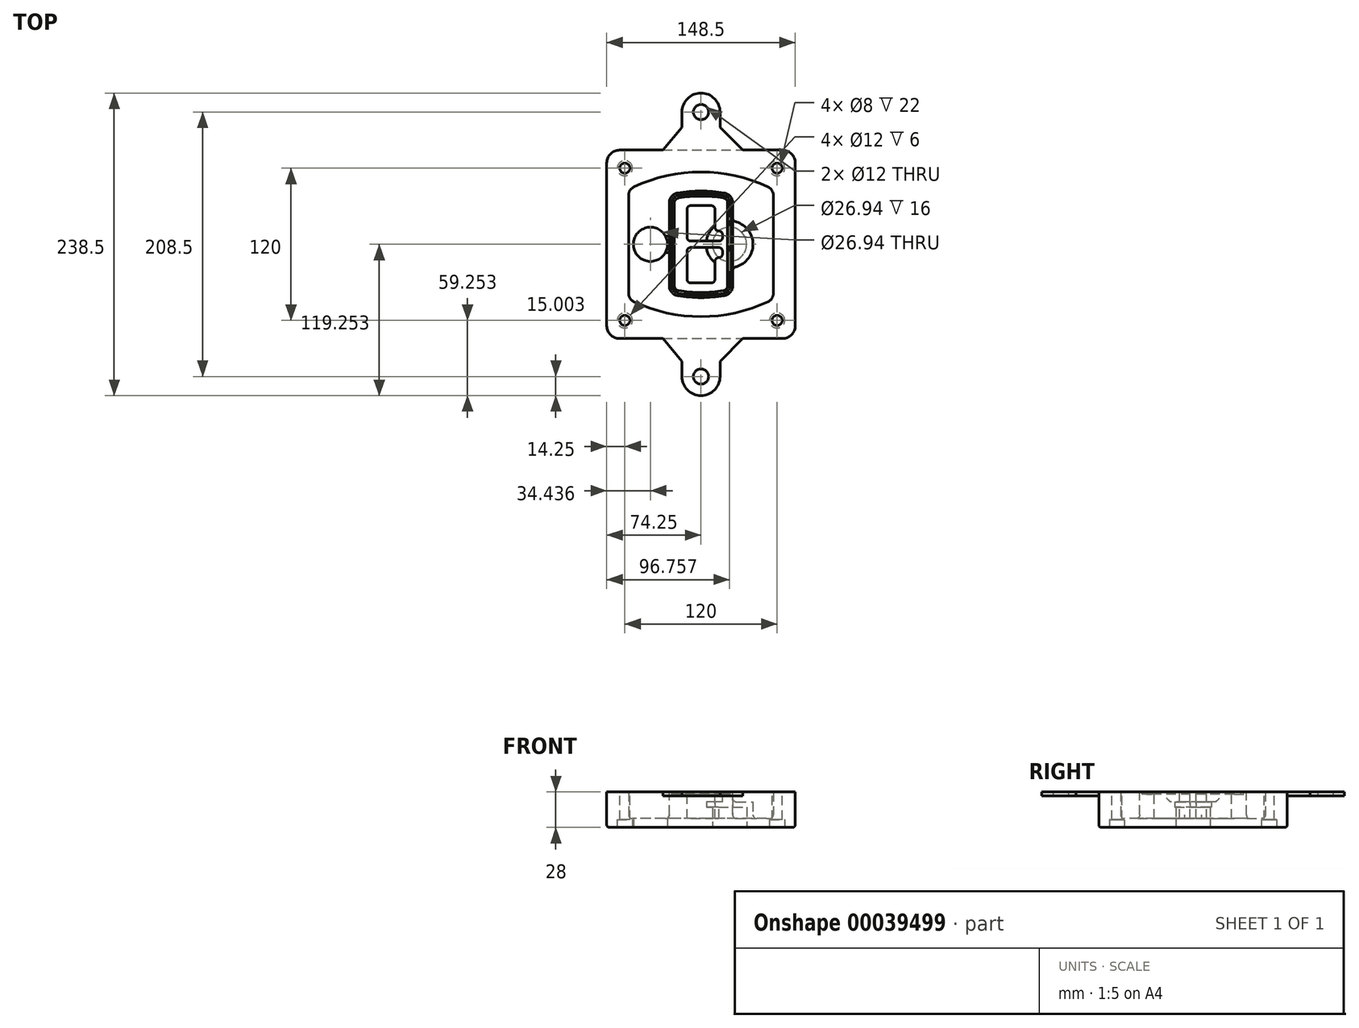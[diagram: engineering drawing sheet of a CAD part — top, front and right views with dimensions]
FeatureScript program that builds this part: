
annotation { "Feature Type Name" : "Feature", "Feature Type Description" : "" }
export const myFeature = defineFeature(function(context is Context, id is Id, definition is map)
    precondition{}
    {
        {
            var Q0;
            Q0=qCreatedBy(makeId("Top.planeOp"),FACE);
            var sketch = newSketch(context, id + "F0", { "sketchPlane" : qUnion([Q0])});
            skPoint(sketch, "E0.rect.middle", {"position": v(0, 0) * mm});
            skLineSegment(sketch, "E1.bottom", {"start": v(24.05, 28.38) * mm, "end": v(152.55, 28.38) * mm});
            skLineSegment(sketch, "E1.top", {"start": v(24.05, 176.88) * mm, "end": v(152.55, 176.88) * mm});
            skLineSegment(sketch, "E1.left", {"start": v(14.05, 38.38) * mm, "end": v(14.05, 166.88) * mm});
            skLineSegment(sketch, "E1.right", {"start": v(162.55, 38.38) * mm, "end": v(162.55, 166.88) * mm});
            skLineSegment(sketch, "E2", {"start": v(14.05, 176.88) * mm, "end": v(162.55, 28.38) * mm, "construction": true});
            skLineSegment(sketch, "E3", {"start": v(162.55, 176.88) * mm, "end": v(14.05, 28.38) * mm, "construction": true});
            skCircle(sketch, "E4", {"center": v(28.3, 162.63) * mm, "radius": 4 * mm});
            skCircle(sketch, "E5", {"center": v(148.3, 162.63) * mm, "radius": 4 * mm});
            skCircle(sketch, "E6", {"center": v(148.3, 42.63) * mm, "radius": 4 * mm});
            skCircle(sketch, "E7", {"center": v(28.3, 42.63) * mm, "radius": 4 * mm});
            skLineSegment(sketch, "E8", {"start": v(28.3, 162.63) * mm, "end": v(148.3, 162.63) * mm, "construction": true});
            skLineSegment(sketch, "E9", {"start": v(148.3, 162.63) * mm, "end": v(148.3, 42.63) * mm, "construction": true});
            skLineSegment(sketch, "E10", {"start": v(148.3, 42.63) * mm, "end": v(28.3, 42.63) * mm, "construction": true});
            skLineSegment(sketch, "E11", {"start": v(28.3, 42.63) * mm, "end": v(28.3, 162.63) * mm, "construction": true});
            skLineSegment(sketch, "E12", {"start": v(28.3, 141.46) * mm, "end": v(28.3, 63.8) * mm});
            skLineSegment(sketch, "E13", {"start": v(148.3, 141.46) * mm, "end": v(148.3, 63.8) * mm});
            skArc(sketch, "E14", {"start": v(142.56, 150.51) * mm, "mid": v(88.3, 162.63) * mm, "end": v(34.04, 150.51) * mm});
            skArc(sketch, "E15", {"start": v(34.04, 54.75) * mm, "mid": v(88.3, 42.63) * mm, "end": v(142.56, 54.75) * mm});
            skLineSegment(sketch, "E16", {"start": v(28.3, 102.63) * mm, "end": v(148.3, 102.63) * mm, "construction": true});
            skPoint(sketch, "E17.visualSharp", {"position": v(28.3, 57.63) * mm});
            skArc(sketch, "E17.filletArc", {"start": v(28.3, 63.8) * mm, "mid": v(29.86, 58.44) * mm, "end": v(34.04, 54.75) * mm});
            skPoint(sketch, "E18.visualSharp", {"position": v(28.3, 147.63) * mm});
            skArc(sketch, "E18.filletArc", {"start": v(34.04, 150.51) * mm, "mid": v(29.86, 146.82) * mm, "end": v(28.3, 141.46) * mm});
            skPoint(sketch, "E19.visualSharp", {"position": v(148.3, 147.63) * mm});
            skArc(sketch, "E19.filletArc", {"start": v(148.3, 141.46) * mm, "mid": v(146.74, 146.82) * mm, "end": v(142.56, 150.51) * mm});
            skPoint(sketch, "E20.visualSharp", {"position": v(148.3, 57.63) * mm});
            skArc(sketch, "E20.filletArc", {"start": v(142.56, 54.75) * mm, "mid": v(146.74, 58.44) * mm, "end": v(148.3, 63.8) * mm});
            skPoint(sketch, "E21.visualSharp", {"position": v(14.05, 176.88) * mm});
            skArc(sketch, "E21.filletArc", {"start": v(24.05, 176.88) * mm, "mid": v(16.98, 173.95) * mm, "end": v(14.05, 166.88) * mm});
            skPoint(sketch, "E22.visualSharp", {"position": v(162.55, 176.88) * mm});
            skArc(sketch, "E22.filletArc", {"start": v(162.55, 166.88) * mm, "mid": v(159.62, 173.95) * mm, "end": v(152.55, 176.88) * mm});
            skPoint(sketch, "E23.visualSharp", {"position": v(162.55, 28.38) * mm});
            skArc(sketch, "E23.filletArc", {"start": v(152.55, 28.38) * mm, "mid": v(159.62, 31.31) * mm, "end": v(162.55, 38.38) * mm});
            skPoint(sketch, "E24.visualSharp", {"position": v(14.05, 28.38) * mm});
            skArc(sketch, "E24.filletArc", {"start": v(14.05, 38.38) * mm, "mid": v(16.98, 31.31) * mm, "end": v(24.05, 28.38) * mm});
            skArc(sketch, "E25.0", {"start": v(145.3, 141.46) * mm, "mid": v(144.2, 145.22) * mm, "end": v(141.28, 147.8) * mm});
            skLineSegment(sketch, "E25.1", {"start": v(145.3, 141.46) * mm, "end": v(145.3, 63.8) * mm});
            skArc(sketch, "E25.2", {"start": v(141.28, 57.47) * mm, "mid": v(144.2, 60.05) * mm, "end": v(145.3, 63.8) * mm});
            skArc(sketch, "E25.3", {"start": v(35.32, 57.47) * mm, "mid": v(88.3, 45.63) * mm, "end": v(141.28, 57.47) * mm});
            skArc(sketch, "E25.4", {"start": v(31.3, 63.8) * mm, "mid": v(32.4, 60.05) * mm, "end": v(35.32, 57.47) * mm});
            skArc(sketch, "E25.5", {"start": v(141.28, 147.8) * mm, "mid": v(88.3, 159.63) * mm, "end": v(35.32, 147.8) * mm});
            skLineSegment(sketch, "E25.6", {"start": v(31.3, 141.46) * mm, "end": v(31.3, 63.8) * mm});
            skArc(sketch, "E25.7", {"start": v(35.32, 147.8) * mm, "mid": v(32.4, 145.22) * mm, "end": v(31.3, 141.46) * mm});
            skArc(sketch, "E26.0", {"start": v(32.34, 154.13) * mm, "mid": v(26.48, 148.97) * mm, "end": v(24.3, 141.46) * mm});
            skArc(sketch, "E26.1", {"start": v(144.26, 154.13) * mm, "mid": v(88.3, 166.63) * mm, "end": v(32.34, 154.13) * mm});
            skArc(sketch, "E26.2", {"start": v(152.3, 141.46) * mm, "mid": v(150.12, 148.97) * mm, "end": v(144.26, 154.13) * mm});
            skLineSegment(sketch, "E26.3", {"start": v(152.3, 141.46) * mm, "end": v(152.3, 63.8) * mm});
            skArc(sketch, "E26.4", {"start": v(144.26, 51.13) * mm, "mid": v(150.12, 56.3) * mm, "end": v(152.3, 63.8) * mm});
            skLineSegment(sketch, "E26.5", {"start": v(24.3, 141.46) * mm, "end": v(24.3, 63.8) * mm});
            skArc(sketch, "E26.6", {"start": v(32.34, 51.13) * mm, "mid": v(88.3, 38.63) * mm, "end": v(144.26, 51.13) * mm});
            skArc(sketch, "E26.7", {"start": v(24.3, 63.8) * mm, "mid": v(26.48, 56.3) * mm, "end": v(32.34, 51.13) * mm});
            skSolve(sketch);
        }
        {
            var Q0;
            Q0=makeQuery(id+"F0.imprint","IMPRINT",FACE,{"disambiguationData":[TD([[makeQuery(id+"F0.imprint","IMPRINT",EDGE,{"derivedFrom":sQuery(id+"F0.wireOp",EDGE,"E1.bottom")}),1.0]])]});
            var Q1;
            Q1=makeQuery(id+"F0.imprint","IMPRINT",FACE,{"disambiguationData":[TD([[makeQuery(id+"F0.imprint","IMPRINT",EDGE,{"derivedFrom":sQuery(id+"F0.wireOp",EDGE,"E12")}),1.0]])]});
            var Q2;
            Q2=makeQuery(id+"F0.imprint","IMPRINT",FACE,{"disambiguationData":[TD([[makeQuery(id+"F0.imprint","IMPRINT",EDGE,{"derivedFrom":sQuery(id+"F0.wireOp",EDGE,"E25.0")}),1.0]])]});
            var Q3;
            Q3=makeQuery(id+"F0.imprint","IMPRINT",FACE,{"disambiguationData":[TD([[makeQuery(id+"F0.imprint","IMPRINT",EDGE,{"derivedFrom":sQuery(id+"F0.wireOp",EDGE,"E12")}),-1.0]])]});
            extrude(context, id + "F1", {"entities" : qUnion([Q0, Q1, Q2, Q3]), "oppositeDirection" : true, "depth" : 25 * mm});
        }
        {
            var Q0;
            Q0=makeQuery(id+"F0.imprint","IMPRINT",FACE,{"disambiguationData":[TD([[makeQuery(id+"F0.imprint","IMPRINT",EDGE,{"derivedFrom":sQuery(id+"F0.wireOp",EDGE,"E12")}),1.0]])]});
            extrude(context, id + "F2", {"entities" : qUnion([Q0]), "operationType" : NewBodyOperationType.ADD, "depth" : 3 * mm});
        }
        {
            var Q0;
            Q0=makeQuery(id+"F0.imprint","IMPRINT",FACE,{"disambiguationData":[TD([[makeQuery(id+"F0.imprint","IMPRINT",EDGE,{"derivedFrom":sQuery(id+"F0.wireOp",EDGE,"E25.0")}),1.0]])]});
            extrude(context, id + "F3", {"entities" : qUnion([Q0]), "operationType" : NewBodyOperationType.REMOVE, "oppositeDirection" : true, "depth" : 18 * mm});
        }
        {
            var Q0;
            Q0=makeQuery(id+"F2.opExtrude","CAP_FACE",FACE,{"disambiguationData":[OSD([sQuery(id+"F0.wireOp",EDGE,"E12"),sQuery(id+"F0.wireOp",EDGE,"E13"),sQuery(id+"F0.wireOp",EDGE,"E14"),sQuery(id+"F0.wireOp",EDGE,"E15"),sQuery(id+"F0.wireOp",EDGE,"E17.filletArc"),sQuery(id+"F0.wireOp",EDGE,"E18.filletArc"),sQuery(id+"F0.wireOp",EDGE,"E19.filletArc"),sQuery(id+"F0.wireOp",EDGE,"E20.filletArc"),sQuery(id+"F0.wireOp",EDGE,"E25.0"),sQuery(id+"F0.wireOp",EDGE,"E25.1"),sQuery(id+"F0.wireOp",EDGE,"E25.2"),sQuery(id+"F0.wireOp",EDGE,"E25.3"),sQuery(id+"F0.wireOp",EDGE,"E25.4"),sQuery(id+"F0.wireOp",EDGE,"E25.5"),sQuery(id+"F0.wireOp",EDGE,"E25.6"),sQuery(id+"F0.wireOp",EDGE,"E25.7")])],"isStart":false});
            var sketch = newSketch(context, id + "F4", { "sketchPlane" : qUnion([Q0])});
            skArc(sketch, "E27.0", {"start": v(69.96, 62.18) * mm, "mid": v(88.3, 60.63) * mm, "end": v(106.64, 62.18) * mm});
            skArc(sketch, "E28.0", {"start": v(106.64, 143.09) * mm, "mid": v(88.3, 144.63) * mm, "end": v(69.96, 143.09) * mm});
            skLineSegment(sketch, "E29", {"start": v(63.3, 135.2) * mm, "end": v(63.3, 70.07) * mm});
            skLineSegment(sketch, "E30", {"start": v(113.3, 135.2) * mm, "end": v(113.3, 70.07) * mm});
            skLineSegment(sketch, "E31", {"start": v(63.3, 141.74) * mm, "end": v(113.3, 141.74) * mm, "construction": true});
            skLineSegment(sketch, "E32", {"start": v(63.3, 63.52) * mm, "end": v(113.3, 63.52) * mm, "construction": true});
            skPoint(sketch, "E33.visualSharp", {"position": v(63.3, 141.74) * mm});
            skArc(sketch, "E33.filletArc", {"start": v(69.96, 143.09) * mm, "mid": v(65.19, 140.36) * mm, "end": v(63.3, 135.2) * mm});
            skPoint(sketch, "E34.visualSharp", {"position": v(113.3, 141.74) * mm});
            skArc(sketch, "E34.filletArc", {"start": v(113.3, 135.2) * mm, "mid": v(111.41, 140.36) * mm, "end": v(106.64, 143.09) * mm});
            skPoint(sketch, "E35.visualSharp", {"position": v(113.3, 63.52) * mm});
            skArc(sketch, "E35.filletArc", {"start": v(106.64, 62.18) * mm, "mid": v(111.41, 64.9) * mm, "end": v(113.3, 70.07) * mm});
            skPoint(sketch, "E36.visualSharp", {"position": v(63.3, 63.52) * mm});
            skArc(sketch, "E36.filletArc", {"start": v(63.3, 70.07) * mm, "mid": v(65.19, 64.9) * mm, "end": v(69.96, 62.18) * mm});
            skArc(sketch, "E37.0", {"start": v(141.28, 147.8) * mm, "mid": v(88.3, 159.63) * mm, "end": v(35.32, 147.8) * mm});
            skArc(sketch, "E37.1", {"start": v(35.32, 147.8) * mm, "mid": v(32.4, 145.22) * mm, "end": v(31.3, 141.46) * mm});
            skLineSegment(sketch, "E37.2", {"start": v(31.3, 141.46) * mm, "end": v(31.3, 63.8) * mm});
            skArc(sketch, "E37.3", {"start": v(31.3, 63.8) * mm, "mid": v(32.4, 60.05) * mm, "end": v(35.32, 57.47) * mm});
            skArc(sketch, "E37.4", {"start": v(35.32, 57.47) * mm, "mid": v(88.3, 45.63) * mm, "end": v(141.28, 57.47) * mm});
            skArc(sketch, "E37.5", {"start": v(141.28, 57.47) * mm, "mid": v(144.2, 60.05) * mm, "end": v(145.3, 63.8) * mm});
            skLineSegment(sketch, "E37.6", {"start": v(145.3, 141.46) * mm, "end": v(145.3, 63.8) * mm});
            skArc(sketch, "E37.7", {"start": v(145.3, 141.46) * mm, "mid": v(144.2, 145.22) * mm, "end": v(141.28, 147.8) * mm});
            skLineSegment(sketch, "E38.0", {"start": v(111.3, 135.2) * mm, "end": v(111.3, 70.07) * mm});
            skArc(sketch, "E38.1", {"start": v(106.3, 64.15) * mm, "mid": v(109.88, 66.2) * mm, "end": v(111.3, 70.07) * mm});
            skArc(sketch, "E38.2", {"start": v(70.3, 64.15) * mm, "mid": v(88.3, 62.63) * mm, "end": v(106.3, 64.15) * mm});
            skArc(sketch, "E38.3", {"start": v(65.3, 70.07) * mm, "mid": v(66.72, 66.2) * mm, "end": v(70.3, 64.15) * mm});
            skLineSegment(sketch, "E38.4", {"start": v(65.3, 135.2) * mm, "end": v(65.3, 70.07) * mm});
            skArc(sketch, "E38.5", {"start": v(111.3, 135.2) * mm, "mid": v(109.88, 139.07) * mm, "end": v(106.3, 141.11) * mm});
            skArc(sketch, "E38.6", {"start": v(70.3, 141.11) * mm, "mid": v(66.72, 139.07) * mm, "end": v(65.3, 135.2) * mm});
            skArc(sketch, "E38.7", {"start": v(106.3, 141.11) * mm, "mid": v(88.3, 142.63) * mm, "end": v(70.3, 141.11) * mm});
            skArc(sketch, "E39.0", {"start": v(109.3, 135.2) * mm, "mid": v(108.36, 137.78) * mm, "end": v(105.97, 139.14) * mm});
            skLineSegment(sketch, "E39.1", {"start": v(109.3, 135.2) * mm, "end": v(109.3, 70.07) * mm});
            skArc(sketch, "E39.2", {"start": v(105.97, 66.12) * mm, "mid": v(108.36, 67.49) * mm, "end": v(109.3, 70.07) * mm});
            skArc(sketch, "E39.3", {"start": v(70.63, 66.12) * mm, "mid": v(88.3, 64.63) * mm, "end": v(105.97, 66.12) * mm});
            skArc(sketch, "E39.4", {"start": v(67.3, 70.07) * mm, "mid": v(68.24, 67.49) * mm, "end": v(70.63, 66.12) * mm});
            skArc(sketch, "E39.5", {"start": v(105.97, 139.14) * mm, "mid": v(88.3, 140.63) * mm, "end": v(70.63, 139.14) * mm});
            skLineSegment(sketch, "E39.6", {"start": v(67.3, 135.2) * mm, "end": v(67.3, 70.07) * mm});
            skArc(sketch, "E39.7", {"start": v(70.63, 139.14) * mm, "mid": v(68.24, 137.78) * mm, "end": v(67.3, 135.2) * mm});
            skLineSegment(sketch, "E40", {"start": v(63.3, 102.63) * mm, "end": v(113.3, 102.63) * mm, "construction": true});
            skLineSegment(sketch, "E41", {"start": v(77.3, 108.13) * mm, "end": v(77.3, 130.13) * mm});
            skLineSegment(sketch, "E42", {"start": v(80.3, 133.13) * mm, "end": v(96.3, 133.13) * mm});
            skLineSegment(sketch, "E43", {"start": v(99.3, 130.13) * mm, "end": v(99.3, 116.13) * mm});
            skLineSegment(sketch, "E44", {"start": v(102.3, 113.13) * mm, "end": v(102.3, 113.13) * mm});
            skLineSegment(sketch, "E45", {"start": v(105.3, 110.13) * mm, "end": v(105.3, 108.13) * mm});
            skLineSegment(sketch, "E46", {"start": v(102.3, 105.13) * mm, "end": v(80.3, 105.13) * mm});
            skPoint(sketch, "E47.visualSharp", {"position": v(77.3, 133.13) * mm});
            skArc(sketch, "E47.filletArc", {"start": v(80.3, 133.13) * mm, "mid": v(78.18, 132.25) * mm, "end": v(77.3, 130.13) * mm});
            skPoint(sketch, "E48.visualSharp", {"position": v(99.3, 133.13) * mm});
            skArc(sketch, "E48.filletArc", {"start": v(99.3, 130.13) * mm, "mid": v(98.42, 132.25) * mm, "end": v(96.3, 133.13) * mm});
            skPoint(sketch, "E49.visualSharp", {"position": v(99.3, 113.13) * mm});
            skArc(sketch, "E49.filletArc", {"start": v(99.3, 116.13) * mm, "mid": v(100.18, 114.01) * mm, "end": v(102.3, 113.13) * mm});
            skPoint(sketch, "E50.visualSharp", {"position": v(105.3, 113.13) * mm});
            skArc(sketch, "E50.filletArc", {"start": v(105.3, 110.13) * mm, "mid": v(104.42, 112.25) * mm, "end": v(102.3, 113.13) * mm});
            skPoint(sketch, "E51.visualSharp", {"position": v(105.3, 105.13) * mm});
            skArc(sketch, "E51.filletArc", {"start": v(102.3, 105.13) * mm, "mid": v(104.42, 106.01) * mm, "end": v(105.3, 108.13) * mm});
            skPoint(sketch, "E52.visualSharp", {"position": v(77.3, 105.13) * mm});
            skArc(sketch, "E52.filletArc", {"start": v(77.3, 108.13) * mm, "mid": v(78.18, 106.01) * mm, "end": v(80.3, 105.13) * mm});
            skLineSegment(sketch, "E53.0.MirrorCS", {"start": v(102.3, 100.13) * mm, "end": v(80.3, 100.13) * mm});
            skArc(sketch, "E54.0.MirrorCS", {"start": v(77.3, 97.13) * mm, "mid": v(78.18, 99.25) * mm, "end": v(80.3, 100.13) * mm});
            skLineSegment(sketch, "E55.0.MirrorCS", {"start": v(77.3, 97.13) * mm, "end": v(77.3, 75.13) * mm});
            skArc(sketch, "E56.0.MirrorCS", {"start": v(80.3, 72.13) * mm, "mid": v(78.18, 73.01) * mm, "end": v(77.3, 75.13) * mm});
            skLineSegment(sketch, "E57.0.MirrorCS", {"start": v(80.3, 72.13) * mm, "end": v(96.3, 72.13) * mm});
            skArc(sketch, "E58.0.MirrorCS", {"start": v(99.3, 75.13) * mm, "mid": v(98.42, 73.01) * mm, "end": v(96.3, 72.13) * mm});
            skLineSegment(sketch, "E59.0.MirrorCS", {"start": v(99.3, 75.13) * mm, "end": v(99.3, 89.13) * mm});
            skArc(sketch, "E60.0.MirrorCS", {"start": v(99.3, 89.13) * mm, "mid": v(100.18, 91.25) * mm, "end": v(102.3, 92.13) * mm});
            skArc(sketch, "E61.0.MirrorCS", {"start": v(105.3, 95.13) * mm, "mid": v(104.42, 93.01) * mm, "end": v(102.3, 92.13) * mm});
            skLineSegment(sketch, "E62.0.MirrorCS", {"start": v(105.3, 95.13) * mm, "end": v(105.3, 97.13) * mm});
            skArc(sketch, "E63.0.MirrorCS", {"start": v(102.3, 100.13) * mm, "mid": v(104.42, 99.25) * mm, "end": v(105.3, 97.13) * mm});
            skSolve(sketch);
        }
        {
            var Q0;
            Q0=makeQuery(id+"F4.imprint","IMPRINT",FACE,{"disambiguationData":[TD([[makeQuery(id+"F4.imprint","IMPRINT",EDGE,{"derivedFrom":sQuery(id+"F4.wireOp",EDGE,"E27.0")}),1.0]])]});
            var Q1;
            Q1=makeQuery(id+"F4.imprint","IMPRINT",FACE,{"disambiguationData":[TD([[makeQuery(id+"F4.imprint","IMPRINT",EDGE,{"derivedFrom":sQuery(id+"F4.wireOp",EDGE,"E38.0")}),-1.0]])]});
            var Q2;
            Q2=makeQuery(id+"F4.imprint","IMPRINT",FACE,{"disambiguationData":[TD([[makeQuery(id+"F4.imprint","IMPRINT",EDGE,{"derivedFrom":sQuery(id+"F4.wireOp",EDGE,"E39.0")}),1.0]])]});
            extrude(context, id + "F5", {"entities" : qUnion([Q0, Q1, Q2]), "operationType" : NewBodyOperationType.ADD, "endBound" : BoundingType.UP_TO_NEXT, "oppositeDirection" : true, "depth" : 25 * mm});
        }
        {
            var Q0;
            Q0=makeQuery(id+"F4.imprint","IMPRINT",FACE,{"disambiguationData":[TD([[makeQuery(id+"F4.imprint","IMPRINT",EDGE,{"derivedFrom":sQuery(id+"F4.wireOp",EDGE,"E38.0")}),-1.0]])]});
            extrude(context, id + "F6", {"entities" : qUnion([Q0]), "operationType" : NewBodyOperationType.REMOVE, "oppositeDirection" : true, "depth" : 2 * mm});
        }
        {
            var Q0;
            Q0=makeQuery(id+"F1.opExtrude","CAP_FACE",FACE,{"disambiguationData":[OSD([sQuery(id+"F0.wireOp",EDGE,"E1.bottom"),sQuery(id+"F0.wireOp",EDGE,"E1.top"),sQuery(id+"F0.wireOp",EDGE,"E1.left"),sQuery(id+"F0.wireOp",EDGE,"E1.right"),sQuery(id+"F0.wireOp",EDGE,"E4"),sQuery(id+"F0.wireOp",EDGE,"E5"),sQuery(id+"F0.wireOp",EDGE,"E6"),sQuery(id+"F0.wireOp",EDGE,"E7"),sQuery(id+"F0.wireOp",EDGE,"E21.filletArc"),sQuery(id+"F0.wireOp",EDGE,"E22.filletArc"),sQuery(id+"F0.wireOp",EDGE,"E23.filletArc"),sQuery(id+"F0.wireOp",EDGE,"E24.filletArc")])],"isStart":false});
            var sketch = newSketch(context, id + "F7", { "sketchPlane" : qUnion([Q0])});
            skCircle(sketch, "E64", {"center": v(110.8, -102.63) * mm, "radius": 13.47 * mm});
            skCircle(sketch, "E65", {"center": v(48.49, -102.63) * mm, "radius": 13.47 * mm});
            skLineSegment(sketch, "E66", {"start": v(162.55, -102.63) * mm, "end": v(14.05, -102.63) * mm});
            skCircle(sketch, "E67", {"center": v(110.8, -102.63) * mm, "radius": 18.47 * mm});
            skCircle(sketch, "E68", {"center": v(148.3, -162.63) * mm, "radius": 6 * mm});
            skCircle(sketch, "E69", {"center": v(28.3, -162.63) * mm, "radius": 6 * mm});
            skCircle(sketch, "E70", {"center": v(28.3, -42.63) * mm, "radius": 6 * mm});
            skCircle(sketch, "E71", {"center": v(148.3, -42.63) * mm, "radius": 6 * mm});
            skSolve(sketch);
        }
        {
            var Q0;
            {var subQ1=sQuery(id+"F7.wireOp",EDGE,"E66");var subQ4=sQuery(id+"F7.wireOp",EDGE,"E64");var subQ6=makeQuery(id+"F7.imprint","INTERSECT",VERTEX,{"disambiguationData":[OD(0.0)],"derivedFrom":[subQ4,subQ1]});Q0=makeQuery(id+"F7.imprint","IMPRINT",FACE,{"disambiguationData":[TD([[makeQuery(id+"F7.imprint","IMPRINT",EDGE,{"disambiguationData":[TD([[subQ6,-1.0]])],"derivedFrom":subQ4}),-1.0]])]});}
            var Q1;
            {var subQ0=sQuery(id+"F7.wireOp",EDGE,"E66");var subQ1=sQuery(id+"F7.wireOp",EDGE,"E64");var subQ3=makeQuery(id+"F7.imprint","INTERSECT",VERTEX,{"disambiguationData":[OD(0.0)],"derivedFrom":[subQ1,subQ0]});Q1=makeQuery(id+"F7.imprint","IMPRINT",FACE,{"disambiguationData":[TD([[makeQuery(id+"F7.imprint","IMPRINT",EDGE,{"disambiguationData":[TD([[subQ3,-1.0]])],"derivedFrom":subQ1}),1.0]])]});}
            var Q2;
            {var subQ0=sQuery(id+"F7.wireOp",EDGE,"E66");var subQ1=sQuery(id+"F7.wireOp",EDGE,"E64");var subQ3=makeQuery(id+"F7.imprint","INTERSECT",VERTEX,{"disambiguationData":[OD(0.0)],"derivedFrom":[subQ1,subQ0]});Q2=makeQuery(id+"F7.imprint","IMPRINT",FACE,{"disambiguationData":[TD([[makeQuery(id+"F7.imprint","IMPRINT",EDGE,{"disambiguationData":[TD([[subQ3,1.0]])],"derivedFrom":subQ1}),1.0]])]});}
            var Q3;
            {var subQ1=sQuery(id+"F7.wireOp",EDGE,"E66");var subQ4=sQuery(id+"F7.wireOp",EDGE,"E64");var subQ6=makeQuery(id+"F7.imprint","INTERSECT",VERTEX,{"disambiguationData":[OD(0.0)],"derivedFrom":[subQ4,subQ1]});Q3=makeQuery(id+"F7.imprint","IMPRINT",FACE,{"disambiguationData":[TD([[makeQuery(id+"F7.imprint","IMPRINT",EDGE,{"disambiguationData":[TD([[subQ6,1.0]])],"derivedFrom":subQ4}),-1.0]])]});}
            extrude(context, id + "F8", {"entities" : qUnion([Q0, Q1, Q2, Q3]), "operationType" : NewBodyOperationType.ADD, "oppositeDirection" : true, "depth" : 20 * mm});
        }
        {
            var Q0;
            {var subQ0=sQuery(id+"F7.wireOp",EDGE,"E66");var subQ1=sQuery(id+"F7.wireOp",EDGE,"E64");var subQ3=makeQuery(id+"F7.imprint","INTERSECT",VERTEX,{"disambiguationData":[OD(0.0)],"derivedFrom":[subQ1,subQ0]});Q0=makeQuery(id+"F7.imprint","IMPRINT",FACE,{"disambiguationData":[TD([[makeQuery(id+"F7.imprint","IMPRINT",EDGE,{"disambiguationData":[TD([[subQ3,-1.0]])],"derivedFrom":subQ1}),1.0]])]});}
            var Q1;
            {var subQ0=sQuery(id+"F7.wireOp",EDGE,"E66");var subQ1=sQuery(id+"F7.wireOp",EDGE,"E64");var subQ3=makeQuery(id+"F7.imprint","INTERSECT",VERTEX,{"disambiguationData":[OD(0.0)],"derivedFrom":[subQ1,subQ0]});Q1=makeQuery(id+"F7.imprint","IMPRINT",FACE,{"disambiguationData":[TD([[makeQuery(id+"F7.imprint","IMPRINT",EDGE,{"disambiguationData":[TD([[subQ3,1.0]])],"derivedFrom":subQ1}),1.0]])]});}
            extrude(context, id + "F9", {"entities" : qUnion([Q0, Q1]), "operationType" : NewBodyOperationType.REMOVE, "oppositeDirection" : true, "depth" : 16 * mm});
        }
        {
            var Q0;
            {var subQ0=sQuery(id+"F7.wireOp",EDGE,"E66");var subQ1=sQuery(id+"F7.wireOp",EDGE,"E65");var subQ3=makeQuery(id+"F7.imprint","INTERSECT",VERTEX,{"disambiguationData":[OD(0.0)],"derivedFrom":[subQ1,subQ0]});Q0=makeQuery(id+"F7.imprint","IMPRINT",FACE,{"disambiguationData":[TD([[makeQuery(id+"F7.imprint","IMPRINT",EDGE,{"disambiguationData":[TD([[subQ3,-1.0]])],"derivedFrom":subQ1}),1.0]])]});}
            var Q1;
            {var subQ0=sQuery(id+"F7.wireOp",EDGE,"E66");var subQ1=sQuery(id+"F7.wireOp",EDGE,"E65");var subQ3=makeQuery(id+"F7.imprint","INTERSECT",VERTEX,{"disambiguationData":[OD(0.0)],"derivedFrom":[subQ1,subQ0]});Q1=makeQuery(id+"F7.imprint","IMPRINT",FACE,{"disambiguationData":[TD([[makeQuery(id+"F7.imprint","IMPRINT",EDGE,{"disambiguationData":[TD([[subQ3,1.0]])],"derivedFrom":subQ1}),1.0]])]});}
            extrude(context, id + "F10", {"entities" : qUnion([Q0, Q1]), "operationType" : NewBodyOperationType.REMOVE, "oppositeDirection" : true, "depth" : 25 * mm});
        }
        {
            var Q0;
            Q0=makeQuery(id+"F7.imprint","IMPRINT",FACE,{"disambiguationData":[TD([[makeQuery(id+"F7.imprint","IMPRINT",EDGE,{"derivedFrom":sQuery(id+"F7.wireOp",EDGE,"E68")}),1.0]])]});
            var Q1;
            Q1=makeQuery(id+"F7.imprint","IMPRINT",FACE,{"disambiguationData":[TD([[makeQuery(id+"F7.imprint","IMPRINT",EDGE,{"derivedFrom":makeQuery(id+"F1.opExtrude","CAP_EDGE",EDGE,{"disambiguationData":[OSD([sQuery(id+"F0.wireOp",EDGE,"E5")])],"isStart":false})}),-1.0]])]});
            var Q2;
            Q2=makeQuery(id+"F7.imprint","IMPRINT",FACE,{"disambiguationData":[TD([[makeQuery(id+"F7.imprint","IMPRINT",EDGE,{"derivedFrom":sQuery(id+"F7.wireOp",EDGE,"E69")}),1.0]])]});
            var Q3;
            Q3=makeQuery(id+"F7.imprint","IMPRINT",FACE,{"disambiguationData":[TD([[makeQuery(id+"F7.imprint","IMPRINT",EDGE,{"derivedFrom":makeQuery(id+"F1.opExtrude","CAP_EDGE",EDGE,{"disambiguationData":[OSD([sQuery(id+"F0.wireOp",EDGE,"E4")])],"isStart":false})}),-1.0]])]});
            var Q4;
            Q4=makeQuery(id+"F7.imprint","IMPRINT",FACE,{"disambiguationData":[TD([[makeQuery(id+"F7.imprint","IMPRINT",EDGE,{"derivedFrom":sQuery(id+"F7.wireOp",EDGE,"E70")}),1.0]])]});
            var Q5;
            Q5=makeQuery(id+"F7.imprint","IMPRINT",FACE,{"disambiguationData":[TD([[makeQuery(id+"F7.imprint","IMPRINT",EDGE,{"derivedFrom":makeQuery(id+"F1.opExtrude","CAP_EDGE",EDGE,{"disambiguationData":[OSD([sQuery(id+"F0.wireOp",EDGE,"E7")])],"isStart":false})}),-1.0]])]});
            var Q6;
            Q6=makeQuery(id+"F7.imprint","IMPRINT",FACE,{"disambiguationData":[TD([[makeQuery(id+"F7.imprint","IMPRINT",EDGE,{"derivedFrom":sQuery(id+"F7.wireOp",EDGE,"E71")}),1.0]])]});
            var Q7;
            Q7=makeQuery(id+"F7.imprint","IMPRINT",FACE,{"disambiguationData":[TD([[makeQuery(id+"F7.imprint","IMPRINT",EDGE,{"derivedFrom":makeQuery(id+"F1.opExtrude","CAP_EDGE",EDGE,{"disambiguationData":[OSD([sQuery(id+"F0.wireOp",EDGE,"E6")])],"isStart":false})}),-1.0]])]});
            extrude(context, id + "F11", {"entities" : qUnion([Q0, Q1, Q2, Q3, Q4, Q5, Q6, Q7]), "operationType" : NewBodyOperationType.REMOVE, "oppositeDirection" : true, "depth" : 6 * mm});
        }
        {
            var Q0;
            Q0=makeQuery(id+"F9.boolean.opBoolean","COPY",FACE,{"derivedFrom":makeQuery(id+"F9.opExtrude","CAP_FACE",FACE,{"disambiguationData":[OSD([sQuery(id+"F7.wireOp",EDGE,"E64")])],"isStart":false})});
            var sketch = newSketch(context, id + "F12", { "sketchPlane" : qUnion([Q0])});
            skArc(sketch, "E72.0", {"start": v(99.3, -88.19) * mm, "mid": v(94.75, -93.5) * mm, "end": v(92.5, -100.13) * mm});
            skArc(sketch, "E72.1", {"start": v(92.5, -105.13) * mm, "mid": v(94.75, -111.76) * mm, "end": v(99.3, -117.08) * mm});
            skLineSegment(sketch, "E73", {"start": v(92.5, -105.13) * mm, "end": v(102.3, -105.13) * mm});
            skLineSegment(sketch, "E74.0", {"start": v(102.3, -100.13) * mm, "end": v(92.5, -100.13) * mm});
            skArc(sketch, "E74.1", {"start": v(102.3, -100.13) * mm, "mid": v(104.42, -99.25) * mm, "end": v(105.3, -97.13) * mm});
            skLineSegment(sketch, "E74.2", {"start": v(105.3, -95.13) * mm, "end": v(105.3, -97.13) * mm});
            skArc(sketch, "E74.3", {"start": v(105.3, -95.13) * mm, "mid": v(104.42, -93.01) * mm, "end": v(102.3, -92.13) * mm});
            skArc(sketch, "E74.4", {"start": v(99.3, -89.13) * mm, "mid": v(100.18, -91.25) * mm, "end": v(102.3, -92.13) * mm});
            skLineSegment(sketch, "E74.5", {"start": v(99.3, -88.19) * mm, "end": v(99.3, -89.13) * mm});
            skLineSegment(sketch, "E74.7", {"start": v(102.3, -105.13) * mm, "end": v(92.5, -105.13) * mm});
            skArc(sketch, "E74.8", {"start": v(102.3, -105.13) * mm, "mid": v(104.42, -106.01) * mm, "end": v(105.3, -108.13) * mm});
            skLineSegment(sketch, "E74.9", {"start": v(105.3, -110.13) * mm, "end": v(105.3, -108.13) * mm});
            skArc(sketch, "E74.10", {"start": v(105.3, -110.13) * mm, "mid": v(104.42, -112.25) * mm, "end": v(102.3, -113.13) * mm});
            skArc(sketch, "E74.11", {"start": v(99.3, -116.13) * mm, "mid": v(100.18, -114.01) * mm, "end": v(102.3, -113.13) * mm});
            skLineSegment(sketch, "E74.12", {"start": v(99.3, -117.08) * mm, "end": v(99.3, -116.13) * mm});
            skPoint(sketch, "E75.orphan", {"position": v(99.3, -130.13) * mm});
            skPoint(sketch, "E76.orphan", {"position": v(80.3, -105.13) * mm});
            skPoint(sketch, "E77.orphan", {"position": v(80.3, -100.13) * mm});
            skPoint(sketch, "E78.orphan", {"position": v(99.3, -75.13) * mm});
            skSolve(sketch);
        }
        {
            var Q0;
            {var subQ7=sQuery(id+"F12.wireOp",EDGE,"E72.0");var subQ14=sQuery(id+"F12.wireOp",EDGE,"E72.1");var subQ16=sQuery(id+"F12.wireOp",EDGE,"E74.1");var subQ18=sQuery(id+"F12.wireOp",EDGE,"E74.8");Q0=qUnion([makeQuery(id+"F12.imprint","IMPRINT",FACE,{"disambiguationData":[TD([[makeQuery(id+"F12.imprint","IMPRINT",EDGE,{"derivedFrom":subQ7}),1.0]])]}),makeQuery(id+"F12.imprint","IMPRINT",FACE,{"disambiguationData":[TD([[makeQuery(id+"F12.imprint","IMPRINT",EDGE,{"derivedFrom":subQ14}),1.0]])]}),makeQuery(id+"F12.imprint","IMPRINT",FACE,{"disambiguationData":[TD([[makeQuery(id+"F12.imprint","IMPRINT",EDGE,{"derivedFrom":subQ16}),1.0]])]}),makeQuery(id+"F12.imprint","IMPRINT",FACE,{"disambiguationData":[TD([[makeQuery(id+"F12.imprint","IMPRINT",EDGE,{"derivedFrom":subQ18}),-1.0]])]})]);}
            var Q1;
            Q1=makeQuery(id+"F5.boolean.opBoolean","SPLIT",FACE,{"disambiguationData":[TD([makeQuery(id+"F5.opExtrude","SWEPT_FACE",FACE,{"disambiguationData":[OSD([sQuery(id+"F4.wireOp",EDGE,"E41")])]})])],"derivedFrom":makeQuery(id+"F3.boolean.opBoolean","COPY",FACE,{"derivedFrom":makeQuery(id+"F3.opExtrude","CAP_FACE",FACE,{"disambiguationData":[OSD([sQuery(id+"F0.wireOp",EDGE,"E25.0"),sQuery(id+"F0.wireOp",EDGE,"E25.1"),sQuery(id+"F0.wireOp",EDGE,"E25.2"),sQuery(id+"F0.wireOp",EDGE,"E25.3"),sQuery(id+"F0.wireOp",EDGE,"E25.4"),sQuery(id+"F0.wireOp",EDGE,"E25.5"),sQuery(id+"F0.wireOp",EDGE,"E25.6"),sQuery(id+"F0.wireOp",EDGE,"E25.7")])],"isStart":false})})});
            extrude(context, id + "F13", {"entities" : qUnion([Q0]), "operationType" : NewBodyOperationType.REMOVE, "endBound" : BoundingType.UP_TO_SURFACE, "endBoundEntityFace" : qUnion([Q1]), "depth" : 25 * mm});
        }
        {
            var Q0;
            Q0=makeQuery(id+"F3.boolean.opBoolean","COPY",EDGE,{"derivedFrom":makeQuery(id+"F3.opExtrude","CAP_EDGE",EDGE,{"disambiguationData":[OSD([sQuery(id+"F0.wireOp",EDGE,"E25.6")])],"isStart":false})});
            var Q1;
            Q1=makeQuery(id+"F8.boolean.opBoolean","INTERSECT",EDGE,{"derivedFrom":[makeQuery(id+"F5.opExtrude","SWEPT_FACE",FACE,{"disambiguationData":[OSD([sQuery(id+"F4.wireOp",EDGE,"E30")])]}),makeQuery(id+"F8.opExtrude","CAP_FACE",FACE,{"disambiguationData":[OSD([sQuery(id+"F7.wireOp",EDGE,"E67")])],"isStart":false})]});
            var Q2;
            Q2=makeQuery(id+"F8.boolean.opBoolean","INTERSECT",EDGE,{"disambiguationData":[OD(1.0)],"derivedFrom":[makeQuery(id+"F5.opExtrude","SWEPT_FACE",FACE,{"disambiguationData":[OSD([sQuery(id+"F4.wireOp",EDGE,"E30")])]}),makeQuery(id+"F8.opExtrude","SWEPT_FACE",FACE,{"disambiguationData":[OSD([sQuery(id+"F7.wireOp",EDGE,"E67")])]})]});
            var Q3;
            {var subQ0=sQuery(id+"F4.wireOp",EDGE,"E30");Q3=makeQuery(id+"F8.boolean.opBoolean","SPLIT",EDGE,{"disambiguationData":[TD([makeQuery(id+"F5.opExtrude","SWEPT_FACE",FACE,{"disambiguationData":[OSD([sQuery(id+"F4.wireOp",EDGE,"E35.filletArc")])]})])],"derivedFrom":makeQuery(id+"F5.opExtrude","CAP_EDGE",EDGE,{"disambiguationData":[OSD([subQ0])],"isStart":false})});}
            var Q4;
            {var subQ0=sQuery(id+"F0.wireOp",EDGE,"E25.7");var subQ1=sQuery(id+"F0.wireOp",EDGE,"E25.1");var subQ2=sQuery(id+"F0.wireOp",EDGE,"E25.6");var subQ3=sQuery(id+"F0.wireOp",EDGE,"E25.5");var subQ4=sQuery(id+"F0.wireOp",EDGE,"E25.4");var subQ5=sQuery(id+"F0.wireOp",EDGE,"E25.0");var subQ6=sQuery(id+"F0.wireOp",EDGE,"E25.2");var subQ7=sQuery(id+"F0.wireOp",EDGE,"E25.3");Q4=makeQuery(id+"F8.boolean.opBoolean","INTERSECT",EDGE,{"derivedFrom":[makeQuery(id+"F5.boolean.opBoolean","SPLIT",FACE,{"disambiguationData":[TD([makeQuery(id+"F2.opExtrude","SWEPT_FACE",FACE,{"disambiguationData":[OSD([subQ5])]})])],"derivedFrom":makeQuery(id+"F3.boolean.opBoolean","COPY",FACE,{"derivedFrom":makeQuery(id+"F3.opExtrude","CAP_FACE",FACE,{"disambiguationData":[OSD([subQ5,subQ1,subQ6,subQ7,subQ4,subQ3,subQ2,subQ0])],"isStart":false})})}),makeQuery(id+"F8.opExtrude","SWEPT_FACE",FACE,{"disambiguationData":[OSD([sQuery(id+"F7.wireOp",EDGE,"E67")])]})]});}
            var Q5;
            Q5=makeQuery(id+"F8.boolean.opBoolean","INTERSECT",EDGE,{"disambiguationData":[OD(0.0)],"derivedFrom":[makeQuery(id+"F5.opExtrude","SWEPT_FACE",FACE,{"disambiguationData":[OSD([sQuery(id+"F4.wireOp",EDGE,"E30")])]}),makeQuery(id+"F8.opExtrude","SWEPT_FACE",FACE,{"disambiguationData":[OSD([sQuery(id+"F7.wireOp",EDGE,"E67")])]})]});
            fillet(context, id + "F14", {"entities" : qUnion([Q0, Q1, Q2, Q3, Q4, Q5]), "radius" : 3 * mm, "tangentPropagation" : true, "allowEdgeOverflow" : false});
        }
        {
            var Q0;
            Q0=makeQuery(id+"F1.opExtrude","CAP_EDGE",EDGE,{"disambiguationData":[OSD([sQuery(id+"F0.wireOp",EDGE,"E1.bottom")])],"isStart":false});
            fillet(context, id + "F15", {"entities" : qUnion([Q0]), "radius" : 2 * mm, "tangentPropagation" : true, "allowEdgeOverflow" : false});
        }
        {
            var Q0;
            {var subQ0=sQuery(id+"F0.wireOp",EDGE,"E1.bottom");var subQ1=sQuery(id+"F0.wireOp",EDGE,"E1.top");var subQ2=sQuery(id+"F0.wireOp",EDGE,"E1.left");var subQ3=sQuery(id+"F0.wireOp",EDGE,"E1.right");var subQ4=sQuery(id+"F0.wireOp",EDGE,"E4");var subQ5=sQuery(id+"F0.wireOp",EDGE,"E5");var subQ6=sQuery(id+"F0.wireOp",EDGE,"E6");var subQ7=sQuery(id+"F0.wireOp",EDGE,"E7");var subQ8=sQuery(id+"F0.wireOp",EDGE,"E21.filletArc");var subQ9=sQuery(id+"F0.wireOp",EDGE,"E22.filletArc");var subQ10=sQuery(id+"F0.wireOp",EDGE,"E23.filletArc");var subQ11=sQuery(id+"F0.wireOp",EDGE,"E24.filletArc");Q0=makeQuery(id+"F2.boolean.opBoolean","SPLIT",FACE,{"disambiguationData":[TD([makeQuery(id+"F1.opExtrude","SWEPT_FACE",FACE,{"disambiguationData":[OSD([subQ0])]})])],"derivedFrom":makeQuery(id+"F1.opExtrude","CAP_FACE",FACE,{"disambiguationData":[OSD([subQ0,subQ1,subQ2,subQ3,subQ4,subQ5,subQ6,subQ7,subQ8,subQ9,subQ10,subQ11])],"isStart":true})});}
            var sketch = newSketch(context, id + "F16", { "sketchPlane" : qUnion([Q0])});
            skLineSegment(sketch, "E79.0", {"start": v(24.05, 176.88) * mm, "end": v(152.55, 176.88) * mm});
            skArc(sketch, "E79.1", {"start": v(24.05, 176.88) * mm, "mid": v(16.98, 173.95) * mm, "end": v(14.05, 166.88) * mm});
            skLineSegment(sketch, "E79.2", {"start": v(14.05, 38.38) * mm, "end": v(14.05, 166.88) * mm});
            skArc(sketch, "E79.3", {"start": v(14.05, 38.38) * mm, "mid": v(16.98, 31.31) * mm, "end": v(24.05, 28.38) * mm});
            skLineSegment(sketch, "E79.4", {"start": v(24.05, 28.38) * mm, "end": v(152.55, 28.38) * mm});
            skArc(sketch, "E79.5", {"start": v(152.55, 28.38) * mm, "mid": v(159.62, 31.31) * mm, "end": v(162.55, 38.38) * mm});
            skLineSegment(sketch, "E79.6", {"start": v(162.55, 38.38) * mm, "end": v(162.55, 166.88) * mm});
            skArc(sketch, "E79.7", {"start": v(162.55, 166.88) * mm, "mid": v(159.62, 173.95) * mm, "end": v(152.55, 176.88) * mm});
            skCircle(sketch, "E79.8", {"center": v(148.3, 162.63) * mm, "radius": 4 * mm});
            skCircle(sketch, "E79.9", {"center": v(28.3, 162.63) * mm, "radius": 4 * mm});
            skCircle(sketch, "E79.10", {"center": v(28.3, 42.63) * mm, "radius": 4 * mm});
            skCircle(sketch, "E79.11", {"center": v(148.3, 42.63) * mm, "radius": 4 * mm});
            skArc(sketch, "E79.12", {"start": v(142.56, 150.51) * mm, "mid": v(88.3, 162.63) * mm, "end": v(34.04, 150.51) * mm});
            skArc(sketch, "E79.13", {"start": v(34.04, 150.51) * mm, "mid": v(29.86, 146.82) * mm, "end": v(28.3, 141.46) * mm});
            skLineSegment(sketch, "E79.14", {"start": v(28.3, 141.46) * mm, "end": v(28.3, 63.8) * mm});
            skArc(sketch, "E79.15", {"start": v(28.3, 63.8) * mm, "mid": v(29.86, 58.44) * mm, "end": v(34.04, 54.75) * mm});
            skArc(sketch, "E79.16", {"start": v(34.04, 54.75) * mm, "mid": v(88.3, 42.63) * mm, "end": v(142.56, 54.75) * mm});
            skArc(sketch, "E79.17", {"start": v(142.56, 54.75) * mm, "mid": v(146.74, 58.44) * mm, "end": v(148.3, 63.8) * mm});
            skLineSegment(sketch, "E79.18", {"start": v(148.3, 141.46) * mm, "end": v(148.3, 63.8) * mm});
            skArc(sketch, "E79.19", {"start": v(148.3, 141.46) * mm, "mid": v(146.74, 146.82) * mm, "end": v(142.56, 150.51) * mm});
            skLineSegment(sketch, "E80", {"start": v(88.3, 170.13) * mm, "end": v(88.3, 206.88) * mm, "construction": true});
            skPoint(sketch, "E80.endSnap0", {"position": v(88.3, 176.88) * mm});
            skCircle(sketch, "E81", {"center": v(88.3, 206.88) * mm, "radius": 6 * mm});
            skLineSegment(sketch, "E82", {"start": v(58.29, 176.88) * mm, "end": v(73.3, 194.88) * mm});
            skLineSegment(sketch, "E83", {"start": v(73.3, 194.88) * mm, "end": v(73.3, 206.88) * mm});
            skLineSegment(sketch, "E84", {"start": v(121.3, 176.88) * mm, "end": v(103.3, 194.88) * mm});
            skLineSegment(sketch, "E85", {"start": v(103.3, 194.88) * mm, "end": v(103.3, 206.88) * mm});
            skArc(sketch, "E86", {"start": v(103.3, 206.88) * mm, "mid": v(88.3, 221.88) * mm, "end": v(73.3, 206.88) * mm});
            skLineSegment(sketch, "E87", {"start": v(14.05, 102.63) * mm, "end": v(162.55, 102.63) * mm, "construction": true});
            skLineSegment(sketch, "E88.MirrorCS", {"start": v(58.29, 28.38) * mm, "end": v(73.3, 10.38) * mm});
            skArc(sketch, "E89.MirrorCS", {"start": v(103.3, -1.62) * mm, "mid": v(88.3, -16.62) * mm, "end": v(73.3, -1.62) * mm});
            skCircle(sketch, "E90.MirrorC", {"center": v(88.3, -1.62) * mm, "radius": 6 * mm});
            skLineSegment(sketch, "E91.MirrorCS", {"start": v(88.3, 35.13) * mm, "end": v(88.3, -1.62) * mm});
            skLineSegment(sketch, "E92.MirrorCS", {"start": v(103.3, 10.38) * mm, "end": v(103.3, -1.62) * mm});
            skLineSegment(sketch, "E93.MirrorCS", {"start": v(121.3, 28.38) * mm, "end": v(103.3, 10.38) * mm});
            skLineSegment(sketch, "E94.MirrorCS", {"start": v(73.3, 10.38) * mm, "end": v(73.3, -1.62) * mm});
            skSolve(sketch);
        }
        {
            var Q0;
            Q0=makeQuery(id+"F16.imprint","IMPRINT",FACE,{"disambiguationData":[TD([[makeQuery(id+"F16.imprint","IMPRINT",EDGE,{"derivedFrom":sQuery(id+"F16.wireOp",EDGE,"E81")}),-1.0]])]});
            var Q1;
            {var subQ5=sQuery(id+"F16.wireOp",EDGE,"E79.1");Q1=makeQuery(id+"F16.imprint","IMPRINT",FACE,{"disambiguationData":[TD([[makeQuery(id+"F16.imprint","IMPRINT",EDGE,{"derivedFrom":subQ5}),1.0]])]});}
            var Q2;
            {var subQ2=sQuery(id+"F16.wireOp",EDGE,"E88.MirrorCS");Q2=makeQuery(id+"F16.imprint","IMPRINT",FACE,{"disambiguationData":[TD([[makeQuery(id+"F16.imprint","IMPRINT",EDGE,{"derivedFrom":subQ2}),1.0]])]});}
            var Q3;
            Q3=makeQuery(id+"F2.opExtrude","CAP_FACE",FACE,{"disambiguationData":[OSD([sQuery(id+"F0.wireOp",EDGE,"E12"),sQuery(id+"F0.wireOp",EDGE,"E13"),sQuery(id+"F0.wireOp",EDGE,"E14"),sQuery(id+"F0.wireOp",EDGE,"E15"),sQuery(id+"F0.wireOp",EDGE,"E17.filletArc"),sQuery(id+"F0.wireOp",EDGE,"E18.filletArc"),sQuery(id+"F0.wireOp",EDGE,"E19.filletArc"),sQuery(id+"F0.wireOp",EDGE,"E20.filletArc"),sQuery(id+"F0.wireOp",EDGE,"E25.0"),sQuery(id+"F0.wireOp",EDGE,"E25.1"),sQuery(id+"F0.wireOp",EDGE,"E25.2"),sQuery(id+"F0.wireOp",EDGE,"E25.3"),sQuery(id+"F0.wireOp",EDGE,"E25.4"),sQuery(id+"F0.wireOp",EDGE,"E25.5"),sQuery(id+"F0.wireOp",EDGE,"E25.6"),sQuery(id+"F0.wireOp",EDGE,"E25.7")])],"isStart":false});
            extrude(context, id + "F17", {"entities" : qUnion([Q0, Q1, Q2]), "operationType" : NewBodyOperationType.ADD, "endBound" : BoundingType.UP_TO_SURFACE, "endBoundEntityFace" : qUnion([Q3]), "depth" : 25 * mm});
        }
    });
